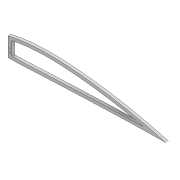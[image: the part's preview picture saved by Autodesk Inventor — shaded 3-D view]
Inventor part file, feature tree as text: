
AUTODESK INVENTOR PART (.ipt)
format: ipt  version: 2022 (Build 260153000, 153)  size: 241,664 bytes
history: native  units: mm
features: sketch x7, extrude x6, thicken_offset x4, projected_geometry x4, shell x1, fillet x1
ambient origin geometry x8: Origin, YZ Plane, XZ Plane, XY Plane, X Axis, Y Axis, Z Axis, Center Point
bodies: Solid1 (feature_tree)
feature tree (23):
  extrude  "Extrusion1"  Depth=5.0mm
  shell  "Shell1"  Thickness=6.0mm
  extrude  "Extrusion2"  Depth=2.0mm
  extrude  "Extrusion3"  Depth=5.9mm
  extrude  "Extrusion4"  Depth=10.0mm TaperAngle=0.0deg
  extrude  "Extrusion7"  Depth=10.0mm TaperAngle=0.0deg
  thicken_offset  "Thicken1"
  thicken_offset  "Thicken2"
  extrude  "Extrusion8"  Depth=2.0mm
  fillet  "Fillet1"  Radius=4.5mm
  thicken_offset  "Thicken4"
  thicken_offset  "Thicken5"
  sketch  "Sketch17"  dims[d31=3.0mm d32=3.0mm d33=3.0mm d34=3.0mm d35=1.0mm d36=10.0mm d37=0.0mm d38=2.0mm d42=0.2mm d43=0.2mm d44=0.2mm d45=0.2mm]
  sketch  "Sketch3"  dims[d0=4.5mm d1=0.0mm d2=5.0mm d3=6.0mm]
  sketch  "Sketch7"  dims[d5=4.5mm d6=0.0mm d7=2.0mm]
  projected_geometry  "Projected Loop3"
  sketch  "Sketch8"  dims[d8=2.0mm d9=5.9mm]
  sketch  "Sketch9"  dims[d12=4.0mm d13=10.0mm d14=0.0mm]
  sketch  "Sketch14"  dims[d15=40.0mm d16=10.0mm d17=0.0mm]
  projected_geometry  "Projected Loop7"
  sketch  "Sketch16"  dims[d24=2.0mm d26=2.0mm d29=4.5mm d30=0.0mm]
  projected_geometry  "Projected Loop9"
  projected_geometry  "Projected Loop10"
